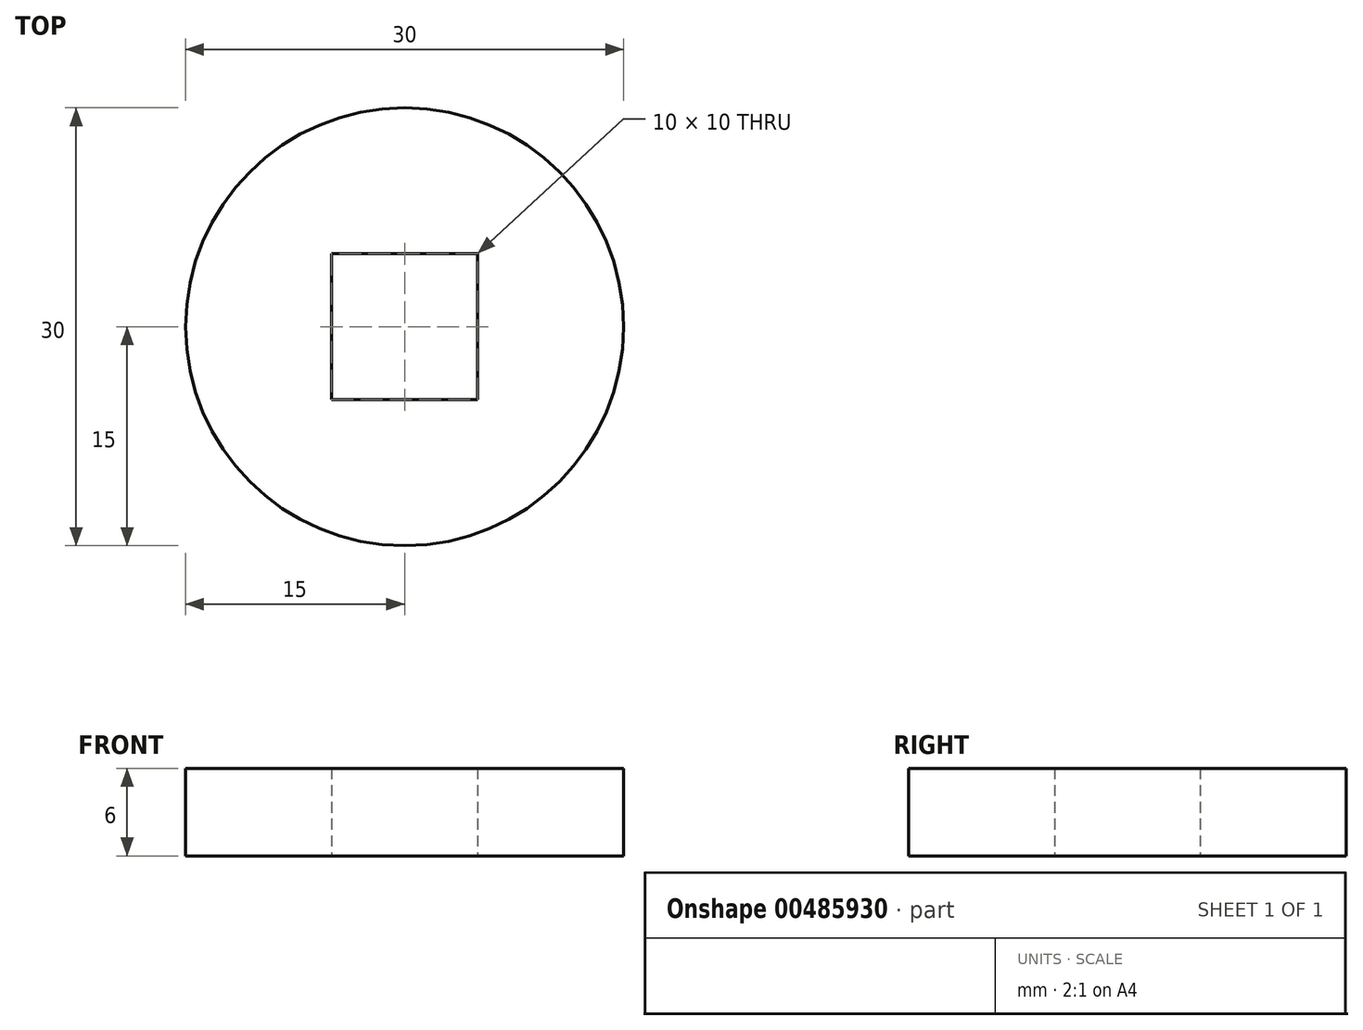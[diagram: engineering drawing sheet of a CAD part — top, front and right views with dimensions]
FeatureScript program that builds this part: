
annotation { "Feature Type Name" : "Feature", "Feature Type Description" : "" }
export const myFeature = defineFeature(function(context is Context, id is Id, definition is map)
    precondition{}
    {
        {
            var Q0;
            Q0=qCreatedBy(makeId("Top.planeOp"),FACE);
            var sketch = newSketch(context, id + "F0", { "sketchPlane" : qUnion([Q0])});
            skCircle(sketch, "E0", {"center": v(0, 0) * mm, "radius": 15 * mm});
            skLineSegment(sketch, "E1.bottom", {"start": v(-5, 5) * mm, "end": v(5, 5) * mm});
            skLineSegment(sketch, "E1.top", {"start": v(-5, -5) * mm, "end": v(5, -5) * mm});
            skLineSegment(sketch, "E1.left", {"start": v(-5, 5) * mm, "end": v(-5, -5) * mm});
            skLineSegment(sketch, "E1.right", {"start": v(5, 5) * mm, "end": v(5, -5) * mm});
            skSolve(sketch);
        }
        {
            var Q0;
            Q0=makeQuery(id+"F0.imprint","IMPRINT",FACE,{"disambiguationData":[TD([[makeQuery(id+"F0.imprint","IMPRINT",EDGE,{"derivedFrom":sQuery(id+"F0.wireOp",EDGE,"E0")}),1.0]])]});
            extrude(context, id + "F1", {"entities" : qUnion([Q0]), "depth" : 6 * mm});
        }
    });
